# Revit family: Workstation-Teknion-Expansion_Casegoods_Private_03-R2012
name_source: partatom
category: Furniture Systems
revit_build: Autodesk Revit Architecture 2013 (Build: 20130531_2115(x64)
units: mm (PartAtom-declared; Revit-internal decimal feet)

## types (1)
- 84" x 108"
    Assembly Code = E2020200
    Depth = 83.7 "
    Description = 7’ x 9’ workstation
    Exposed Plastic Back Note = Outer Back Finish only applies to the Exposed Plastic Back product options
    Height = 65.165 "
    Manufacturer = Teknion
    Manufacturer Fax = 416.661.4586
    Model = Expansion Casegoods - Private 03
    Product Line = Expansion Casegoods
    Product Page URL = http://teknionplanningtool.com
    Single Upholstered Note = Same fabric to be applied to seat and inside back
    Sustainability Data = http://www.teknion.com
    URL = http://www.teknion.com
    Unit Weight URL = http://www.teknion.com
    Warranty = http://www.teknion.com
    Width = 125.52 "

## geometry (parser evidence)
native form markers: Blend x47, Sweep x21
no freeform markers — native parametric forms only
